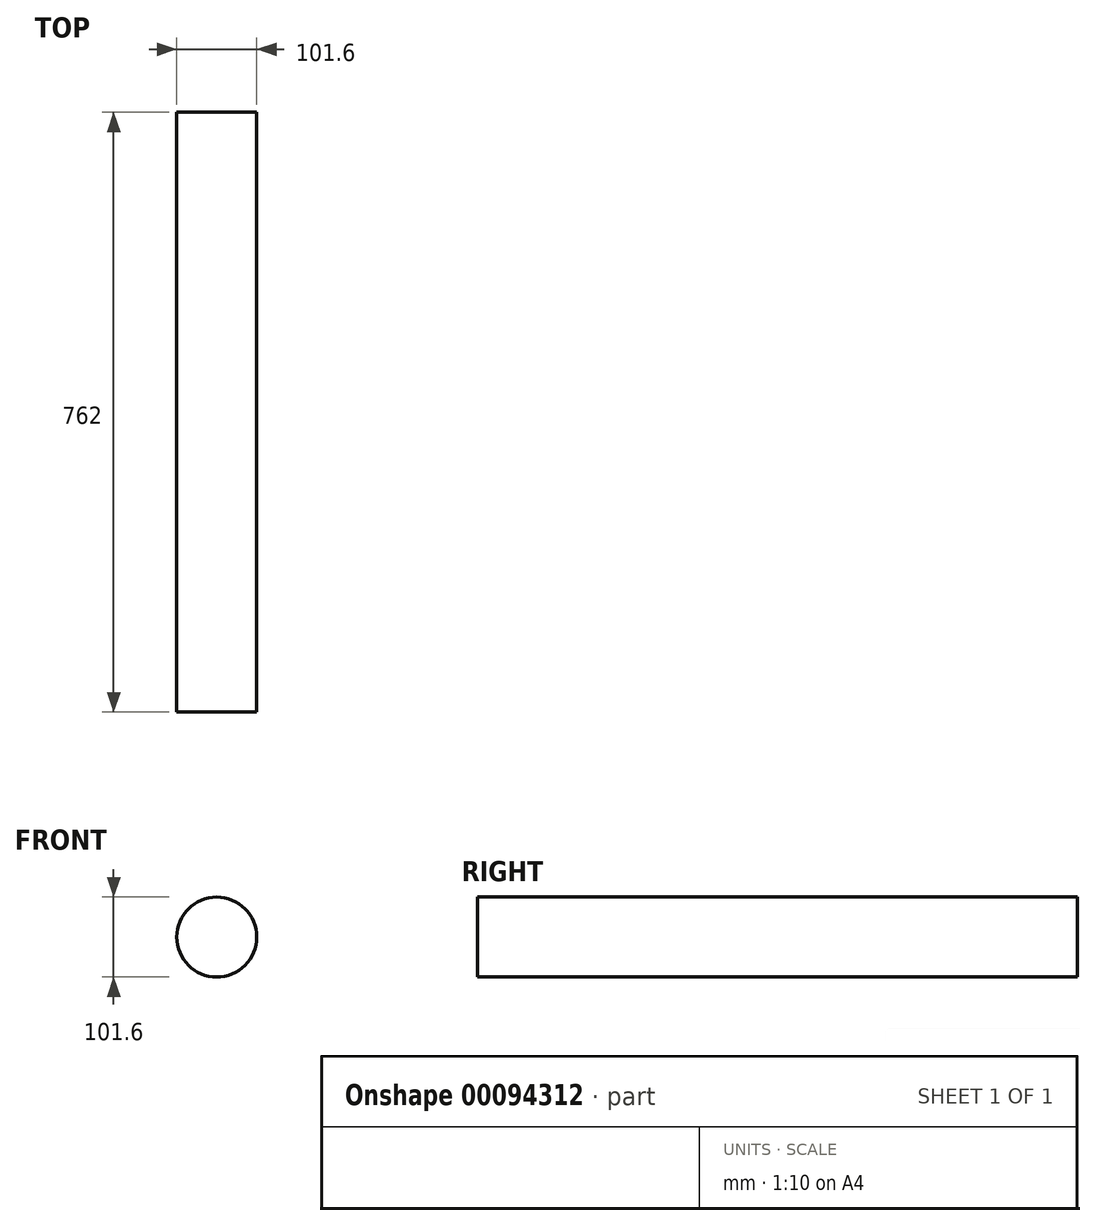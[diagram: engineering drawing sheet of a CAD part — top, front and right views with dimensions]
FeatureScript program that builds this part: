
annotation { "Feature Type Name" : "Feature", "Feature Type Description" : "" }
export const myFeature = defineFeature(function(context is Context, id is Id, definition is map)
    precondition{}
    {
        {
            var Q0;
            Q0=qCreatedBy(makeId("Front.planeOp"),FACE);
            var sketch = newSketch(context, id + "F0", { "sketchPlane" : qUnion([Q0])});
            skCircle(sketch, "E0", {"center": v(0, 0) * mm, "radius": 50.8 * mm});
            skSolve(sketch);
        }
        {
            var Q0;
            Q0 = qSketchRegion(id + "F0", true);
            extrude(context, id + "F1", {"entities" : qUnion([Q0]), "endBound" : BoundingType.SYMMETRIC, "depth" : 762 * mm});
        }
    });
